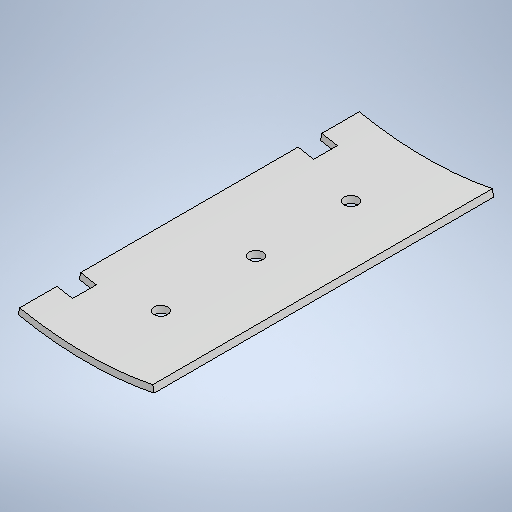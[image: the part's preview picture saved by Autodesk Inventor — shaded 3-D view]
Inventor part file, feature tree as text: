
AUTODESK INVENTOR PART (.ipt)
format: ipt  version: 2025 (Build 290162010, 162A)  size: 271,872 bytes
history: native  units: mm
features: sketch x3, extrude x2, plane x1, hole x1, projected_geometry x1
ambient origin geometry x8: Origin, YZ Plane, XZ Plane, XY Plane, X Axis, Y Axis, Z Axis, Center Point
bodies: Solid1 (feature_tree)
feature tree (8):
  extrude  "Extrusion1"  Depth=101.0mm
  plane  "Work Plane1"
  hole  "Hole1"  [1 undecoded]
  extrude  "Extrusion2"  [1 undecoded]
  sketch  "Sketch1"  dims[d0=2.0mm d1=101.0mm]
  sketch  "Sketch2"  dims[d2=40.0mm d3=99.0mm]
  projected_geometry  "Projected Loop1"
  sketch  "Sketch3"  dims[d4=100.0mm d5=0.0mm d6=-101.0mm d7=22.0mm d8=22.0mm d9=28.0mm d10=28.0mm d11=4.0mm d12=6.0mm d13=4.0mm d14=2.0mm d15=90.0deg d16=8.0mm d17=20.594885mm d18=7.0mm d19=5.0mm d20=11.0mm d21=5.0mm d22=11.0mm d23=7.0mm d24=100.0mm d25=0.0mm]
note: 2 required parameter values undecoded (feature->parameter linkage not recoverable at this tier; creation-order binding heuristic only, values carry confidence <= 0.55)
